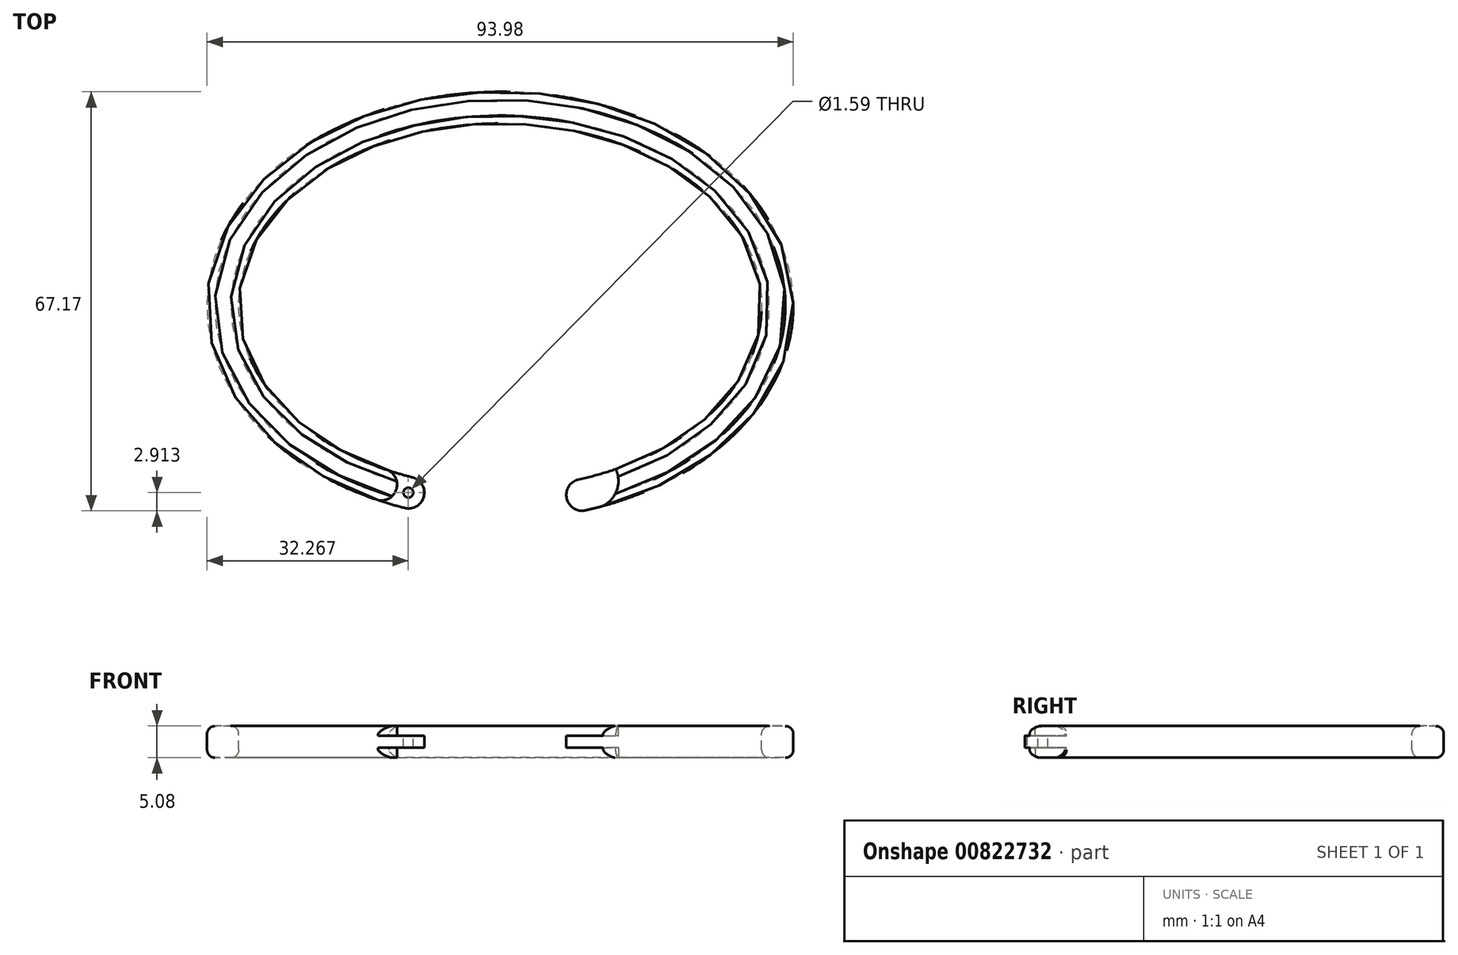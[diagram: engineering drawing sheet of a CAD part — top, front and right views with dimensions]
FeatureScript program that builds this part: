
annotation { "Feature Type Name" : "Feature", "Feature Type Description" : "" }
export const myFeature = defineFeature(function(context is Context, id is Id, definition is map)
    precondition{}
    {
        {
            var Q0;
            Q0=qCreatedBy(makeId("Top.planeOp"),FACE);
            var sketch = newSketch(context, id + "F0", { "sketchPlane" : qUnion([Q0])});
            skEllipticalArc(sketch, "E0", {});
            skEllipticalArc(sketch, "E1", {});
            skEllipticalArc(sketch, "E2", {});
            skArc(sketch, "E3", {"start": v(-15.75, -32.3) * mm, "mid": v(-12.26, -30.66) * mm, "end": v(-14.38, -27.44) * mm});
            skArc(sketch, "E4", {"start": v(12.26, -27.93) * mm, "mid": v(10.77, -31.23) * mm, "end": v(14.07, -32.72) * mm});
            const initialGuessF0  = {"E0": [0, 0, 1, 0, 0.04699, 0.03429, 5.000648409136641, 4.389030351331796], "E1": [0, 0, 1, 0, 0.04445, 0.03175, 4.954456505395508, 4.433631162312573], "E2": [0, 0, 1, 0, 0.04191, 0.02921, 5.009210639362233, 4.375845155550827]};
            skSetInitialGuess(sketch, initialGuessF0);
            skSolve(sketch);
        }
        {
            var Q0;
            {var subQ6=sQuery(id+"F0.wireOp",EDGE,"E1");Q0=makeQuery(id+"F0.imprint","IMPRINT",FACE,{"disambiguationData":[TD([[makeQuery(id+"F0.imprint","IMPRINT",EDGE,{"derivedFrom":subQ6}),1.0]])]});}
            var Q1;
            {var subQ0=sQuery(id+"F0.wireOp",EDGE,"E1");Q1=makeQuery(id+"F0.imprint","IMPRINT",FACE,{"disambiguationData":[TD([[makeQuery(id+"F0.imprint","IMPRINT",EDGE,{"derivedFrom":subQ0}),-1.0]])]});}
            var Q2;
            Q2 = qSketchRegion(id + "F3", true);
            extrude(context, id + "F1", {"entities" : qUnion([Q0, Q1, Q2]), "depth" : 5.08 * mm, "offsetDistance" : 25.4 * mm});
        }
        {
            var Q0;
            Q0=makeQuery(id+"F1.opExtrude","SWEPT_FACE",FACE,{"disambiguationData":[OSD([sQuery(id+"F0.wireOp",EDGE,"E2")])]});
            var Q1;
            Q1=makeQuery(id+"F1.opExtrude","SWEPT_FACE",FACE,{"disambiguationData":[OSD([sQuery(id+"F0.wireOp",EDGE,"E0")])]});
            var Q2;
            Q2=makeQuery(id+"F1.opExtrude","SWEPT_FACE",FACE,{"disambiguationData":[OSD([sQuery(id+"F0.wireOp",EDGE,"E3")])]});
            var Q3;
            Q3=makeQuery(id+"F1.opExtrude","SWEPT_FACE",FACE,{"disambiguationData":[OSD([sQuery(id+"F0.wireOp",EDGE,"E4")])]});
            fillet(context, id + "F2", {"entities" : qUnion([Q0, Q1, Q2, Q3]), "radius" : 1.27 * mm, "tangentPropagation" : true, "allowEdgeOverflow" : false});
        }
        {
            var Q0;
            Q0=makeQuery(id+"F1.opExtrude","CAP_FACE",FACE,{"disambiguationData":[OSD([sQuery(id+"F0.wireOp",EDGE,"E0"),sQuery(id+"F0.wireOp",EDGE,"E2"),sQuery(id+"F0.wireOp",EDGE,"E3"),sQuery(id+"F0.wireOp",EDGE,"E4")])],"isStart":false});
            var sketch = newSketch(context, id + "F3", { "sketchPlane" : qUnion([Q0])});
            skEllipticalArc(sketch, "E5", {});
            skEllipticalArc(sketch, "E6", {});
            skArc(sketch, "E7", {"start": v(-19.56, -31.18) * mm, "mid": v(-16.67, -29.51) * mm, "end": v(-17.9, -26.41) * mm});
            skArc(sketch, "E8", {"start": v(16.52, -32.1) * mm, "mid": v(18.7, -29.55) * mm, "end": v(18.54, -26.2) * mm});
            const initialGuessF3  = {"E5": [0, 0, 1, 0, 0.04191, 0.02921, 4.2712472188748905, 5.170681346269406], "E6": [0, 0, 1, 0, 0.04699, 0.03429, 4.2830331089926865, 5.071588590795385]};
            skSetInitialGuess(sketch, initialGuessF3);
            skSolve(sketch);
        }
        {
            var Q0;
            Q0=qCreatedBy(makeId("Top.planeOp"),FACE);
            var sketch = newSketch(context, id + "F4", { "sketchPlane" : qUnion([Q0])});
            skEllipticalArc(sketch, "E9", {});
            skEllipticalArc(sketch, "E10", {});
            skArc(sketch, "E11", {"start": v(-19.56, -31.18) * mm, "mid": v(-16.67, -29.51) * mm, "end": v(-17.9, -26.41) * mm});
            skArc(sketch, "E12", {"start": v(16.52, -32.1) * mm, "mid": v(18.7, -29.55) * mm, "end": v(18.54, -26.2) * mm});
            const initialGuessF4  = {"E9": [8.199813044881821e-07, -6.832406566487093e-07, 1, 0, 0.04191, 0.02921, 4.2712472188748905, 5.170681346267891], "E10": [8.199813044881821e-07, -6.832406566487093e-07, 1, 0, 0.04699, 0.03429, 4.2830331089926865, 5.071588590795385]};
            skSetInitialGuess(sketch, initialGuessF4);
            skSolve(sketch);
        }
        {
            var Q0;
            {var subQ11=sQuery(id+"F3.wireOp",EDGE,"E5");Q0=makeQuery(id+"F3.imprint","IMPRINT",FACE,{"disambiguationData":[TD([[makeQuery(id+"F3.imprint","IMPRINT",EDGE,{"derivedFrom":subQ11}),-1.0]])]});}
            var Q1;
            {var subQ1=sQuery(id+"F0.wireOp",EDGE,"E3");var subQ2=sQuery(id+"F0.wireOp",EDGE,"E2");var subQ3=sQuery(id+"F0.wireOp",EDGE,"E0");var subQ4=makeQuery(id+"F1.opExtrude","CAP_FACE",FACE,{"disambiguationData":[OSD([subQ3,subQ2,subQ1,sQuery(id+"F0.wireOp",EDGE,"E4")])],"isStart":false});var subQ9=makeQuery(id+"F2.opFillet","BLEND_EDGE",EDGE,{"blendedFrom":[makeQuery(id+"F1.opExtrude","CAP_EDGE",EDGE,{"disambiguationData":[OSD([subQ1])],"isStart":false}),subQ4],"blendedInto":[subQ4]});Q1=makeQuery(id+"F3.imprint","IMPRINT",FACE,{"disambiguationData":[TD([[makeQuery(id+"F3.imprint","IMPRINT",EDGE,{"derivedFrom":subQ9}),1.0]])]});}
            var Q2;
            {var subQ1=sQuery(id+"F0.wireOp",EDGE,"E4");var subQ2=sQuery(id+"F0.wireOp",EDGE,"E2");var subQ3=sQuery(id+"F0.wireOp",EDGE,"E0");var subQ4=makeQuery(id+"F1.opExtrude","CAP_FACE",FACE,{"disambiguationData":[OSD([subQ3,subQ2,sQuery(id+"F0.wireOp",EDGE,"E3"),subQ1])],"isStart":false});var subQ9=makeQuery(id+"F2.opFillet","BLEND_EDGE",EDGE,{"blendedFrom":[makeQuery(id+"F1.opExtrude","CAP_EDGE",EDGE,{"disambiguationData":[OSD([subQ1])],"isStart":false}),subQ4],"blendedInto":[subQ4]});Q2=makeQuery(id+"F3.imprint","IMPRINT",FACE,{"disambiguationData":[TD([[makeQuery(id+"F3.imprint","IMPRINT",EDGE,{"derivedFrom":subQ9}),1.0]])]});}
            extrude(context, id + "F5", {"entities" : qUnion([Q0, Q1, Q2]), "operationType" : NewBodyOperationType.REMOVE, "oppositeDirection" : true, "depth" : 1.59 * mm, "offsetDistance" : 25.4 * mm});
        }
        {
            var Q0;
            Q0=makeQuery(id+"F4.imprint","IMPRINT",FACE,{"disambiguationData":[TD([[makeQuery(id+"F4.imprint","IMPRINT",EDGE,{"derivedFrom":sQuery(id+"F4.wireOp",EDGE,"E9")}),-1.0]])]});
            extrude(context, id + "F6", {"entities" : qUnion([Q0]), "operationType" : NewBodyOperationType.REMOVE, "depth" : 1.59 * mm, "offsetDistance" : 25.4 * mm});
        }
        {
            var Q0;
            {var subQ0=sQuery(id+"F0.wireOp",EDGE,"E3");var subQ3=sQuery(id+"F3.wireOp",EDGE,"E7");Q0=makeQuery(id+"F5.boolean.opBoolean","COPY",FACE,{"disambiguationData":[TD([makeQuery(id+"F1.opExtrude","SWEPT_FACE",FACE,{"disambiguationData":[OSD([subQ0])]})])],"derivedFrom":makeQuery(id+"F5.opExtrude","CAP_FACE",FACE,{"disambiguationData":[OSD([sQuery(id+"F3.wireOp",EDGE,"E5"),sQuery(id+"F3.wireOp",EDGE,"E6"),subQ3,sQuery(id+"F3.wireOp",EDGE,"E8")])],"isStart":false})});}
            var sketch = newSketch(context, id + "F7", { "sketchPlane" : qUnion([Q0])});
            skPoint(sketch, "E13.1", {"position": v(-14.72, -29.97) * mm});
            skSolve(sketch);
        }
        {
            var Q0;
            Q0=sQuery(id+"F7.wireOp",VERTEX,"E13.1");
            var Q1;
            Q1=makeQuery(id+"F1.opExtrude","SWEPT_BODY",BODY,{"disambiguationData":[OSD([sQuery(id+"F0.wireOp",EDGE,"E0"),sQuery(id+"F0.wireOp",EDGE,"E2"),sQuery(id+"F0.wireOp",EDGE,"E3"),sQuery(id+"F0.wireOp",EDGE,"E4")])]});
            hole(context, id + "F8", {"style" : HoleStyle.SIMPLE, "endStyle" : HoleEndStyle.BLIND, "holeDiameter" : 1.59 * mm, "majorDiameter" : 6.35 * mm, "holeDepth" : 7.62 * mm, "isTappedThrough" : true, "tappedDepth" : 12.7 * mm, "tapClearance" : 3, "locations" : qUnion([Q0]), "scope" : qUnion([Q1])});
        }
    });
